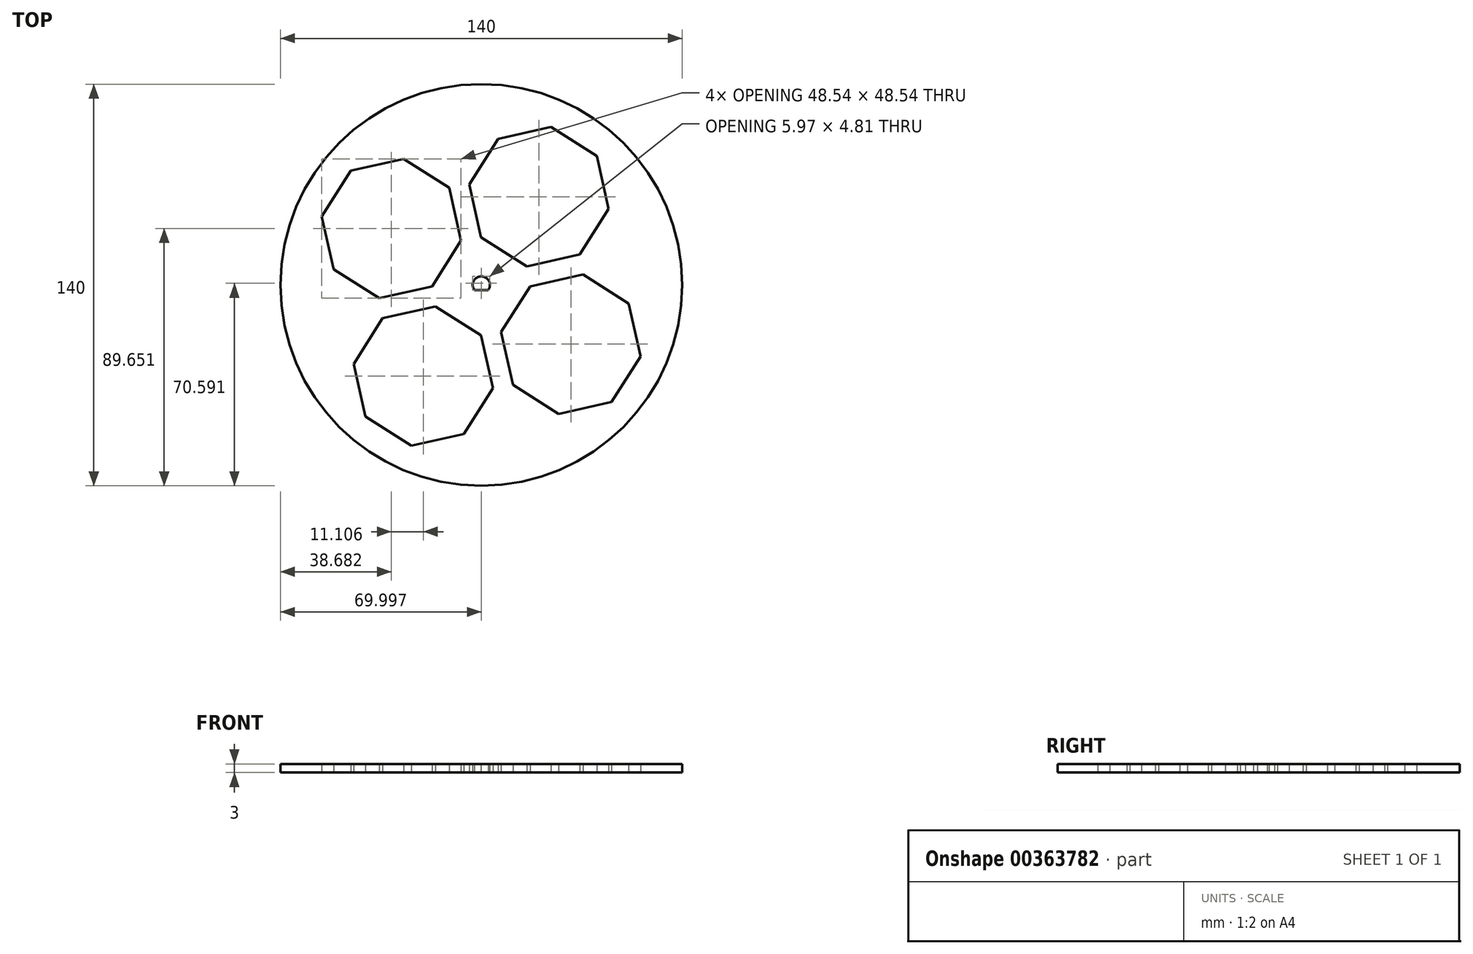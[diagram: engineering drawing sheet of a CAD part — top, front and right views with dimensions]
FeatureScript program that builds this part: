
annotation { "Feature Type Name" : "Feature", "Feature Type Description" : "" }
export const myFeature = defineFeature(function(context is Context, id is Id, definition is map)
    precondition{}
    {
        {
            var Q0;
            Q0=qCreatedBy(makeId("Top.planeOp"),FACE);
            var sketch = newSketch(context, id + "F0", { "sketchPlane" : qUnion([Q0])});
            skCircle(sketch, "E0", {"center": v(0.06, 0.5) * mm, "radius": 70 * mm});
            skCircle(sketch, "E1", {"center": v(0.06, 0.5) * mm, "radius": 3 * mm});
            skCircle(sketch, "E2.cCircle", {"center": v(20.15, 31.26) * mm, "radius": 22.76 * mm, "construction": true});
            skLineSegment(sketch, "E2.0", {"start": v(-4.12, 35.48) * mm, "end": v(5.98, 51.4) * mm});
            skLineSegment(sketch, "E2.1", {"start": v(5.98, 51.4) * mm, "end": v(24.38, 55.53) * mm});
            skLineSegment(sketch, "E2.2", {"start": v(24.38, 55.53) * mm, "end": v(40.3, 45.43) * mm});
            skLineSegment(sketch, "E2.3", {"start": v(40.3, 45.43) * mm, "end": v(44.42, 27.03) * mm});
            skLineSegment(sketch, "E2.4", {"start": v(44.42, 27.03) * mm, "end": v(34.33, 11.1) * mm});
            skLineSegment(sketch, "E2.5", {"start": v(34.33, 11.1) * mm, "end": v(15.93, 6.99) * mm});
            skLineSegment(sketch, "E2.6", {"start": v(15.93, 6.99) * mm, "end": v(0, 17.08) * mm});
            skLineSegment(sketch, "E2.7", {"start": v(0, 17.08) * mm, "end": v(-4.12, 35.48) * mm});
            skPoint(sketch, "E2.0.midPoint", {"position": v(0.93, 43.45) * mm});
            skLineSegment(sketch, "E3.1.0", {"start": v(-27.03, 44.42) * mm, "end": v(-11.1, 34.33) * mm});
            skCircle(sketch, "E3.1.1", {"center": v(-31.26, 20.15) * mm, "radius": 22.76 * mm, "construction": true});
            skLineSegment(sketch, "E3.1.2", {"start": v(-35.48, -4.12) * mm, "end": v(-51.4, 5.98) * mm});
            skLineSegment(sketch, "E3.1.3", {"start": v(-51.4, 5.98) * mm, "end": v(-55.53, 24.38) * mm});
            skLineSegment(sketch, "E3.1.4", {"start": v(-6.99, 15.93) * mm, "end": v(-17.08, 0) * mm});
            skLineSegment(sketch, "E3.1.5", {"start": v(-55.53, 24.38) * mm, "end": v(-45.43, 40.3) * mm});
            skLineSegment(sketch, "E3.1.6", {"start": v(-45.43, 40.3) * mm, "end": v(-27.03, 44.42) * mm});
            skLineSegment(sketch, "E3.1.7", {"start": v(-17.08, 0) * mm, "end": v(-35.48, -4.12) * mm});
            skPoint(sketch, "E3.1.8", {"position": v(-43.45, 0.93) * mm});
            skLineSegment(sketch, "E3.1.9", {"start": v(-11.1, 34.33) * mm, "end": v(-6.99, 15.93) * mm});
            skLineSegment(sketch, "E3.2.0", {"start": v(-44.42, -27.03) * mm, "end": v(-34.33, -11.1) * mm});
            skCircle(sketch, "E3.2.1", {"center": v(-20.15, -31.26) * mm, "radius": 22.76 * mm, "construction": true});
            skLineSegment(sketch, "E3.2.2", {"start": v(4.12, -35.48) * mm, "end": v(-5.98, -51.4) * mm});
            skLineSegment(sketch, "E3.2.3", {"start": v(-5.98, -51.4) * mm, "end": v(-24.38, -55.53) * mm});
            skLineSegment(sketch, "E3.2.4", {"start": v(-15.93, -6.99) * mm, "end": v(0, -17.08) * mm});
            skLineSegment(sketch, "E3.2.5", {"start": v(-24.38, -55.53) * mm, "end": v(-40.3, -45.43) * mm});
            skLineSegment(sketch, "E3.2.6", {"start": v(-40.3, -45.43) * mm, "end": v(-44.42, -27.03) * mm});
            skLineSegment(sketch, "E3.2.7", {"start": v(0, -17.08) * mm, "end": v(4.12, -35.48) * mm});
            skPoint(sketch, "E3.2.8", {"position": v(-0.93, -43.45) * mm});
            skLineSegment(sketch, "E3.2.9", {"start": v(-34.33, -11.1) * mm, "end": v(-15.93, -6.99) * mm});
            skLineSegment(sketch, "E3.3.0", {"start": v(27.03, -44.42) * mm, "end": v(11.1, -34.33) * mm});
            skCircle(sketch, "E3.3.1", {"center": v(31.26, -20.15) * mm, "radius": 22.76 * mm, "construction": true});
            skLineSegment(sketch, "E3.3.2", {"start": v(35.48, 4.12) * mm, "end": v(51.4, -5.98) * mm});
            skLineSegment(sketch, "E3.3.3", {"start": v(51.4, -5.98) * mm, "end": v(55.53, -24.38) * mm});
            skLineSegment(sketch, "E3.3.4", {"start": v(6.99, -15.93) * mm, "end": v(17.08, 0) * mm});
            skLineSegment(sketch, "E3.3.5", {"start": v(55.53, -24.38) * mm, "end": v(45.43, -40.3) * mm});
            skLineSegment(sketch, "E3.3.6", {"start": v(45.43, -40.3) * mm, "end": v(27.03, -44.42) * mm});
            skLineSegment(sketch, "E3.3.7", {"start": v(17.08, 0) * mm, "end": v(35.48, 4.12) * mm});
            skPoint(sketch, "E3.3.8", {"position": v(43.45, -0.93) * mm});
            skLineSegment(sketch, "E3.3.9", {"start": v(11.1, -34.33) * mm, "end": v(6.99, -15.93) * mm});
            skPoint(sketch, "E3.center", {"position": v(0, 0) * mm});
            skSolve(sketch);
        }
        {
            var Q0;
            Q0 = qSketchRegion(id + "F0", true);
            extrude(context, id + "F1", {"entities" : qUnion([Q0]), "endBound" : BoundingType.SYMMETRIC, "depth" : 3 * mm});
        }
        {
            var Q0;
            Q0=qCreatedBy(makeId("Top.planeOp"),FACE);
            var sketch = newSketch(context, id + "F2", { "sketchPlane" : qUnion([Q0])});
            skLineSegment(sketch, "E4.bottom", {"start": v(-2.89, -5.75) * mm, "end": v(2.83, -5.75) * mm});
            skLineSegment(sketch, "E4.top", {"start": v(-2.89, -1.31) * mm, "end": v(2.83, -1.31) * mm});
            skLineSegment(sketch, "E4.left", {"start": v(-2.89, -5.75) * mm, "end": v(-2.89, -1.31) * mm});
            skLineSegment(sketch, "E4.right", {"start": v(2.83, -5.75) * mm, "end": v(2.83, -1.31) * mm});
            skSolve(sketch);
        }
        {
            var Q0;
            Q0=makeQuery(id+"F2.imprint","IMPRINT",FACE,{"disambiguationData":[TD([[makeQuery(id+"F2.imprint","IMPRINT",EDGE,{"derivedFrom":sQuery(id+"F2.wireOp",EDGE,"E4.bottom")}),1.0]])]});
            extrude(context, id + "F3", {"entities" : qUnion([Q0]), "operationType" : NewBodyOperationType.ADD, "endBound" : BoundingType.SYMMETRIC, "depth" : 3 * mm});
        }
    });
